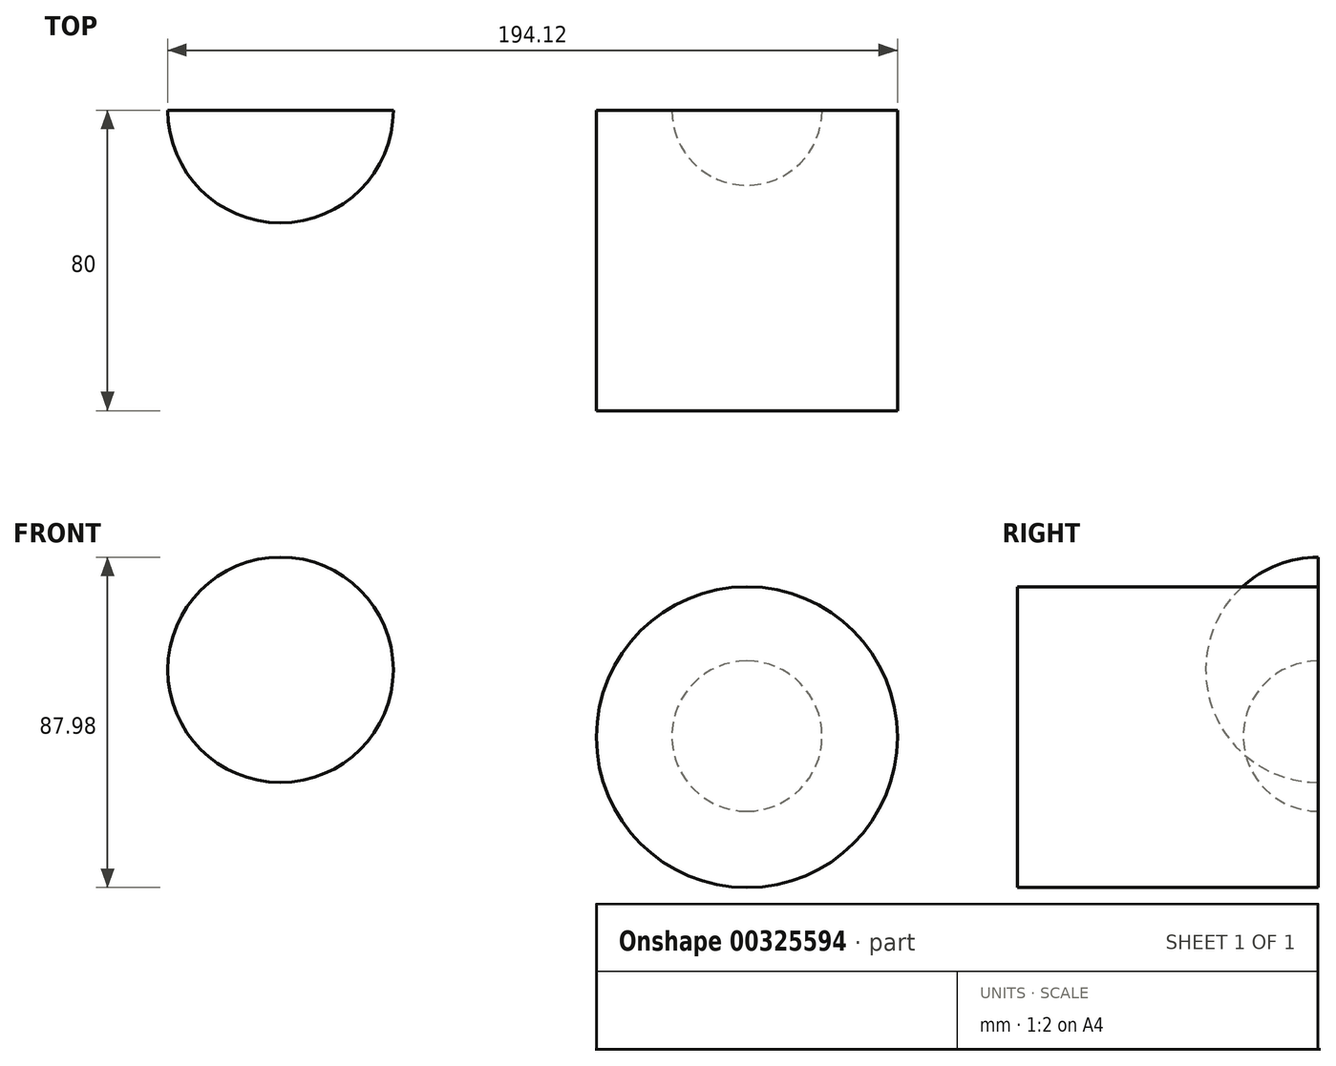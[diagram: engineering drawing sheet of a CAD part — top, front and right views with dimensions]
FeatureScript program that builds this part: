
annotation { "Feature Type Name" : "Feature", "Feature Type Description" : "" }
export const myFeature = defineFeature(function(context is Context, id is Id, definition is map)
    precondition{}
    {
        {
            var Q0;
            Q0=qCreatedBy(makeId("Front.planeOp"),FACE);
            var sketch = newSketch(context, id + "F0", { "sketchPlane" : qUnion([Q0])});
            skCircle(sketch, "E0", {"center": v(0, 0) * mm, "radius": 40.04 * mm});
            skSolve(sketch);
        }
        {
            var Q0;
            Q0 = qSketchRegion(id + "F0", true);
            extrude(context, id + "F1", {"entities" : qUnion([Q0]), "depth" : 80 * mm});
        }
        {
            var Q0;
            Q0=qCreatedBy(makeId("Front.planeOp"),FACE);
            var sketch = newSketch(context, id + "F2", { "sketchPlane" : qUnion([Q0])});
            skLineSegment(sketch, "E1", {"start": v(0, -19.71) * mm, "end": v(0, 20.29) * mm});
            skArc(sketch, "E2", {"start": v(0, -19.71) * mm, "mid": v(20, 0.29) * mm, "end": v(0, 20.29) * mm});
            skSolve(sketch);
        }
        {
            var Q0;
            Q0 = qSketchRegion(id + "F2", true);
            var Q1;
            Q1=sQuery(id+"F2.wireOp",EDGE,"E2");
            var Q2;
            Q2=sQuery(id+"F2.wireOp",EDGE,"E1");
            revolve(context, id + "F3", {"operationType" : NewBodyOperationType.REMOVE, "entities" : qUnion([Q0]), "surfaceEntities" : qUnion([Q1]), "axis" : qUnion([Q2]), "revolveType" : RevolveType.FULL, "oppositeDirection" : true});
        }
        {
            var Q0;
            Q0=qCreatedBy(makeId("Front.planeOp"),FACE);
            var sketch = newSketch(context, id + "F4", { "sketchPlane" : qUnion([Q0])});
            skLineSegment(sketch, "E3", {"start": v(0, -24.35) * mm, "end": v(0, 25.65) * mm});
            skArc(sketch, "E4", {"start": v(0, 25.65) * mm, "mid": v(-25, 0.65) * mm, "end": v(0, -24.35) * mm});
            skSolve(sketch);
        }
        {
            var Q0;
            Q0=sQuery(id+"F4.wireOp",EDGE,"E4");
            var Q1;
            Q1=sQuery(id+"F4.wireOp",EDGE,"E3");
            revolve(context, id + "F5", {"bodyType" : ToolBodyType.SURFACE, "surfaceEntities" : qUnion([Q0]), "axis" : qUnion([Q1]), "revolveType" : RevolveType.FULL});
        }
        {
            var Q0;
            Q0=qCreatedBy(makeId("Front.planeOp"),FACE);
            var sketch = newSketch(context, id + "F6", { "sketchPlane" : qUnion([Q0])});
            skLineSegment(sketch, "E5", {"start": v(-124.08, -12.06) * mm, "end": v(-124.08, 47.94) * mm});
            skArc(sketch, "E6", {"start": v(-124.08, 47.94) * mm, "mid": v(-154.08, 17.94) * mm, "end": v(-124.08, -12.06) * mm});
            skSolve(sketch);
        }
        {
            var Q0;
            Q0=makeQuery(id+"F6.imprint","IMPRINT",FACE,{"disambiguationData":[TD([[makeQuery(id+"F6.imprint","IMPRINT",EDGE,{"derivedFrom":sQuery(id+"F6.wireOp",EDGE,"E5")}),1.0]])]});
            var Q1;
            Q1=sQuery(id+"F6.wireOp",EDGE,"E5");
            revolve(context, id + "F7", {"entities" : qUnion([Q0]), "axis" : qUnion([Q1]), "revolveType" : RevolveType.ONE_DIRECTION, "angle" : 180 * degree});
        }
    });
